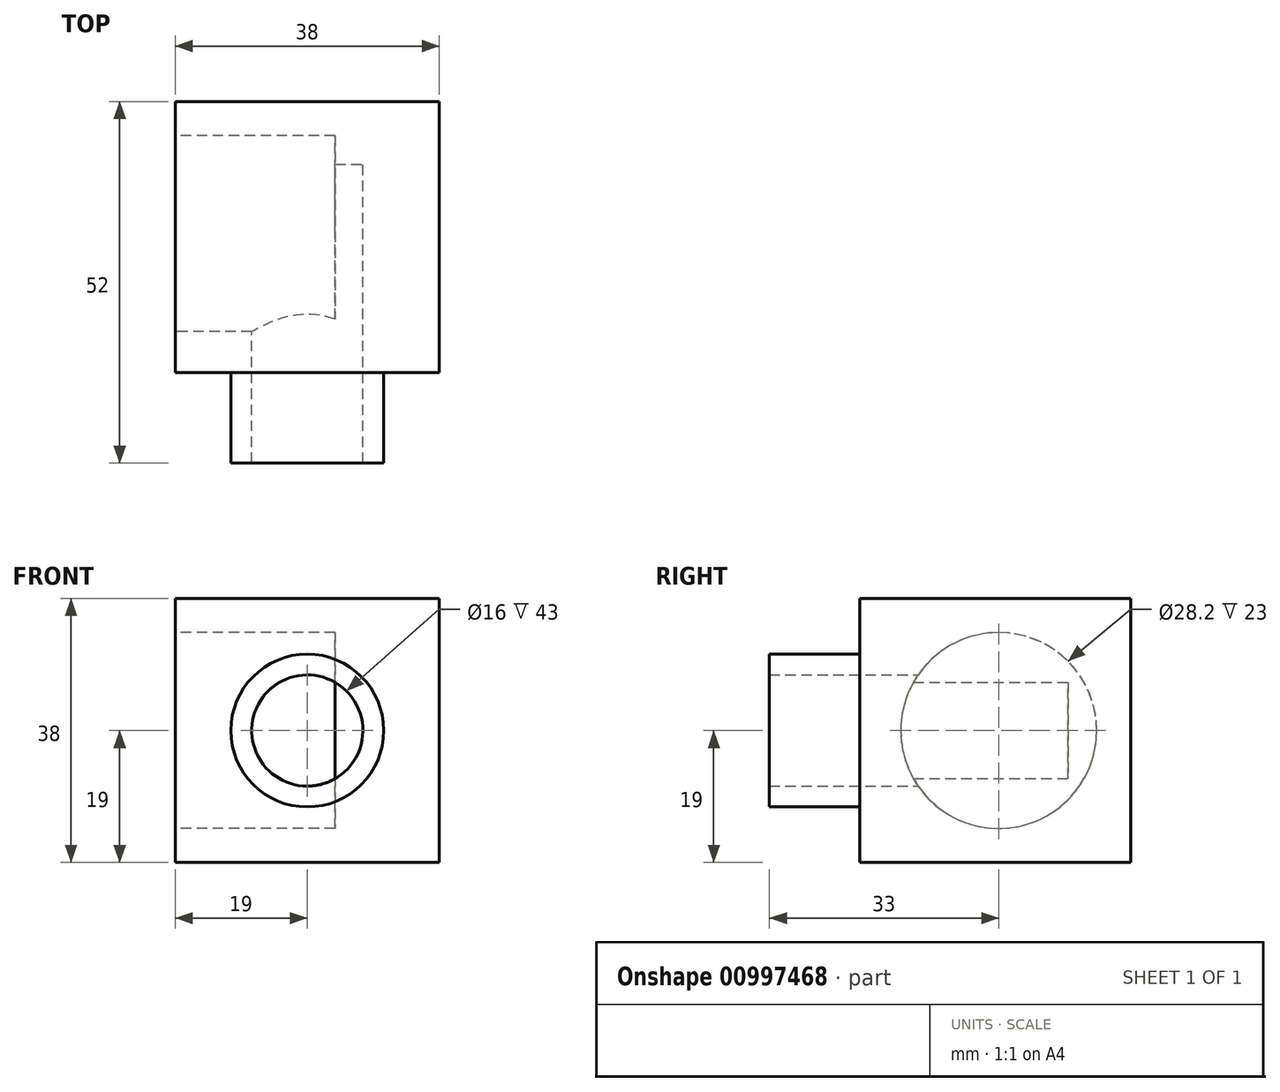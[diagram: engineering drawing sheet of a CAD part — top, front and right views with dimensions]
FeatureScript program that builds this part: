
annotation { "Feature Type Name" : "Feature", "Feature Type Description" : "" }
export const myFeature = defineFeature(function(context is Context, id is Id, definition is map)
    precondition{}
    {
        {
            var Q0;
            Q0=qCreatedBy(makeId("Front.planeOp"),FACE);
            var sketch = newSketch(context, id + "F0", { "sketchPlane" : qUnion([Q0])});
            skLineSegment(sketch, "E0.bottom", {"start": v(-19, 19) * mm, "end": v(19, 19) * mm});
            skLineSegment(sketch, "E0.top", {"start": v(-19, -19) * mm, "end": v(19, -19) * mm});
            skLineSegment(sketch, "E0.left", {"start": v(-19, 19) * mm, "end": v(-19, -19) * mm});
            skLineSegment(sketch, "E0.right", {"start": v(19, 19) * mm, "end": v(19, -19) * mm});
            skSolve(sketch);
        }
        {
            var Q0;
            Q0=makeQuery(id+"F0.imprint","IMPRINT",FACE,{"disambiguationData":[TD([[makeQuery(id+"F0.imprint","IMPRINT",EDGE,{"derivedFrom":sQuery(id+"F0.wireOp",EDGE,"E0.bottom")}),-1.0]])]});
            extrude(context, id + "F1", {"entities" : qUnion([Q0]), "depth" : 39 * mm, "offsetDistance" : 25 * mm});
        }
        {
            var Q0;
            Q0=makeQuery(id+"F1.opExtrude","CAP_FACE",FACE,{"disambiguationData":[OSD([sQuery(id+"F0.wireOp",EDGE,"E0.bottom"),sQuery(id+"F0.wireOp",EDGE,"E0.top"),sQuery(id+"F0.wireOp",EDGE,"E0.left"),sQuery(id+"F0.wireOp",EDGE,"E0.right")])],"isStart":false});
            var sketch = newSketch(context, id + "F2", { "sketchPlane" : qUnion([Q0])});
            skCircle(sketch, "E1", {"center": v(0, 0) * mm, "radius": 11 * mm});
            skCircle(sketch, "E2", {"center": v(0, 0) * mm, "radius": 8 * mm});
            skSolve(sketch);
        }
        {
            var Q0;
            Q0=makeQuery(id+"F2.imprint","IMPRINT",FACE,{"disambiguationData":[TD([[makeQuery(id+"F2.imprint","IMPRINT",EDGE,{"derivedFrom":sQuery(id+"F2.wireOp",EDGE,"E1")}),1.0]])]});
            extrude(context, id + "F3", {"entities" : qUnion([Q0]), "operationType" : NewBodyOperationType.ADD, "depth" : 13 * mm, "offsetDistance" : 25 * mm});
        }
        {
            var Q0;
            Q0=makeQuery(id+"F3.boolean.opBoolean","SPLIT",FACE,{"disambiguationData":[TD([makeQuery(id+"F3.opExtrude","SWEPT_FACE",FACE,{"disambiguationData":[OSD([sQuery(id+"F2.wireOp",EDGE,"E2")])]})])],"derivedFrom":makeQuery(id+"F1.opExtrude","CAP_FACE",FACE,{"disambiguationData":[OSD([sQuery(id+"F0.wireOp",EDGE,"E0.bottom"),sQuery(id+"F0.wireOp",EDGE,"E0.top"),sQuery(id+"F0.wireOp",EDGE,"E0.left"),sQuery(id+"F0.wireOp",EDGE,"E0.right")])],"isStart":false})});
            var sketch = newSketch(context, id + "F4", { "sketchPlane" : qUnion([Q0])});
            skCircle(sketch, "E3", {"center": v(0, 0) * mm, "radius": 8 * mm});
            skSolve(sketch);
        }
        {
            var Q0;
            Q0 = qSketchRegion(id + "F4", true);
            extrude(context, id + "F5", {"entities" : qUnion([Q0]), "operationType" : NewBodyOperationType.REMOVE, "oppositeDirection" : true, "depth" : 30 * mm, "offsetDistance" : 25 * mm});
        }
        {
            var Q0;
            Q0=makeQuery(id+"F1.opExtrude","SWEPT_FACE",FACE,{"disambiguationData":[OSD([sQuery(id+"F0.wireOp",EDGE,"E0.left")])]});
            var sketch = newSketch(context, id + "F6", { "sketchPlane" : qUnion([Q0])});
            skCircle(sketch, "E4", {"center": v(19, 0) * mm, "radius": 14.1 * mm});
            skSolve(sketch);
        }
        {
            var Q0;
            Q0=makeQuery(id+"F6.imprint","IMPRINT",FACE,{"disambiguationData":[TD([[makeQuery(id+"F6.imprint","IMPRINT",EDGE,{"derivedFrom":sQuery(id+"F6.wireOp",EDGE,"E4")}),1.0]])]});
            extrude(context, id + "F7", {"entities" : qUnion([Q0]), "operationType" : NewBodyOperationType.REMOVE, "oppositeDirection" : true, "depth" : 23 * mm, "offsetDistance" : 25 * mm});
        }
    });
